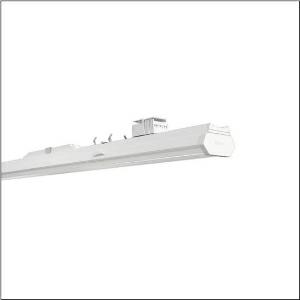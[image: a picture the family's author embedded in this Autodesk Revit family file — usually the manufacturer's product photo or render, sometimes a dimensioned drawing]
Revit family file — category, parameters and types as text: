
# Revit family: licross_r__11_protected_mo_51tp12dn695g_2e2e
name_source: partatom
category: Lighting Fixtures
units: mm (PartAtom-declared; Revit-internal decimal feet)

## family parameters
Cut with Voids When Loaded = No
Host = Face
Light Source = No
Part Type = Normal
Room Calculation Point = No
Round Connector Dimension = Use Diameter
Shared = No

## types (1)
- --- (1 x LED, 9730 lm, 57.1 W, 6500K)
    Apparent Load = 57 VA
    CIE Flux Codes = 73 92 98 99 100
    Color Rendering = 80
    Color Temperature = 6500K
    Default Elevation = 1800 mm
    Description = Licross® 11 Protected MO, luminaire insert, of sheet steel, galvanised, coil coated, white, length: 1.500mm, width: 90mm, height: 101mm, LED rated luminous flux: 9.730lm, light colour: 865, control gear: DALI 2, with plug, 5-pole, with phase selection, mains connection: 220..240V, AC, 50/60Hz, rated input power: 57W, halogen-free wiring, primary optical cover: cover, of PMMA, light emission: direct distribution, primary light characteristic: symmetric, protection rating (complete): IP64, insulation class (complete): insulation class I (protective earthing), certification: CE, ENEC, VDE, UKCA, protection symbol: D if used in an environment with conductive dust loads with corresponding accessories, impact resistance: IK06, permissible ambient temperature for indoor applications: -25..+35°C, corresponds to IFS (International Featured Standards) requirements for safety and quality in the food industry, reducing of maximum allowable ambient temperature of 5°C with ceiling mounting, LABS conformity tested according to VDMA 24364:2018-05, packaging unit: 1 piece
    Height = 92 mm
    Lamp = 1 x LED
    Lamp Light Flux = 9730 lm
    Lamp Power = 57.1 W
    Lamp count = 1
    Length = 1500 mm
    Luminous efficacy = 170 lm/W
    Manufacturer = Siteco
    ModVariant = No
    Model = 51TP12DN695G
    Mounting Place = Ceiling
    Mounting Type = Pendant
    Number of Poles = 1
    OnlyDefault = Yes
    Power Factor = 1
    Product Name = Licross® 11 Protected MO
    Product group = luminaire insert
    ProductGroupID = 902
    Protection Class = Protection class I
    Protection Degree = IP 64
    RLX_Detail_Level = 1
    RLX_Emergency_Light_Flux = 0 lm
    RLX_Emergency_Type = 0
    RLX_Emergency_Type_DB = No
    RlxData = <blob elided: 24429 chars, md5=ec528cd4>
    Socket = socket
    Standby Power = 0 W
    System Light Flux = 9730 lm
    System Power = 57 W
    Type Comments = factory setting: luminous flux: 100 % | dim-lin: 254 | 378 mA
    Type Image = l_1256148.jpg
    URL = http://relux.com
    VarID = @adj_077570
    Voltage = 0 V
    Weight = 0.00 kg
    Width = 88 mm

## geometry (parser evidence)
native form markers: Blend x4, Sweep x11
no freeform markers — native parametric forms only
